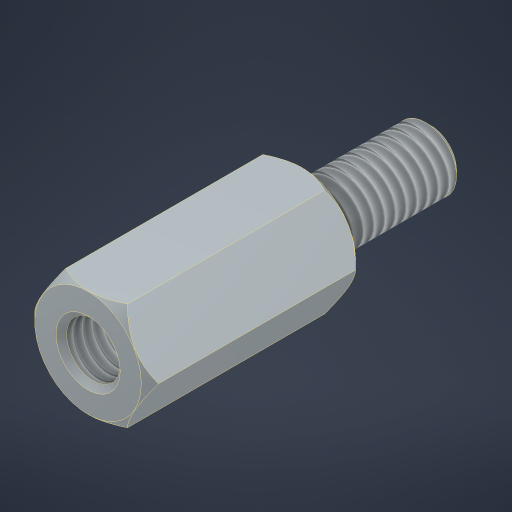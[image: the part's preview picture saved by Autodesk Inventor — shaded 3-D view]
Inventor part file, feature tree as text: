
AUTODESK INVENTOR PART (.ipt)
format: ipt  version: 2023 (Build 270158000, 158)  size: 262,144 bytes
history: native  units: in
note: dims shown in document units (in); Inventor stores cm internally (conversion verified against a paired STEP export)
features: thread x2, other x1
ambient origin geometry x8: Origin, YZ Plane, XZ Plane, XY Plane, X Axis, Y Axis, Z Axis, Center Point
bodies: Solid1 (feature_tree)
feature tree (3):
  thread  "Thread1"  [1 undecoded]
  thread  "Thread2"  [1 undecoded]
  other  "InnerChamfer"
note: 2 required parameter values undecoded (feature->parameter linkage not recoverable at this tier; creation-order binding heuristic only, values carry confidence <= 0.55)
